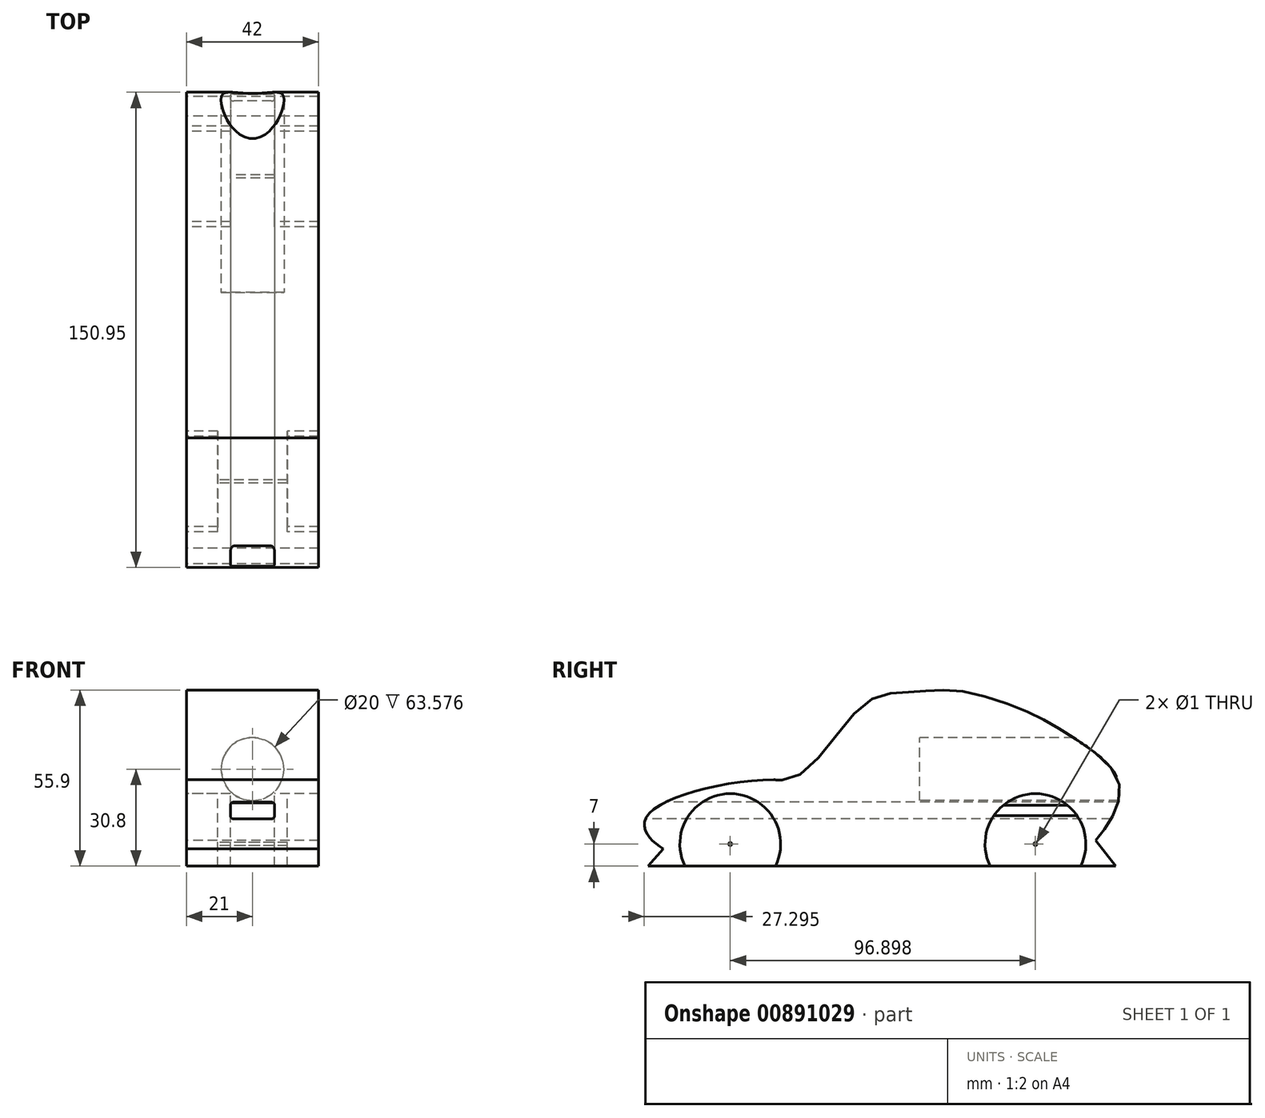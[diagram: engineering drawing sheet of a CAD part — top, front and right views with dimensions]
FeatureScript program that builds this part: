
annotation { "Feature Type Name" : "Feature", "Feature Type Description" : "" }
export const myFeature = defineFeature(function(context is Context, id is Id, definition is map)
    precondition{}
    {
        {
            var Q0;
            Q0=qCreatedBy(makeId("Right.planeOp"),FACE);
            var sketch = newSketch(context, id + "F0", { "sketchPlane" : qUnion([Q0])});
            skArc(sketch, "E0", {"start": v(63.2, 0) * mm, "mid": v(48.81, 23) * mm, "end": v(34.43, 0) * mm});
            skCircle(sketch, "E1", {"center": v(48.81, 7) * mm, "radius": 0.5 * mm});
            skLineSegment(sketch, "E2", {"start": v(-74.19, 0) * mm, "end": v(-69.32, 5.42) * mm});
            skLineSegment(sketch, "E3", {"start": v(74.24, 0) * mm, "end": v(68, 8.2) * mm});
            skLineSegment(sketch, "E4", {"start": v(34.43, 0) * mm, "end": v(63.2, 0) * mm});
            skLineSegment(sketch, "E5", {"start": v(63.2, 0) * mm, "end": v(74.24, 0) * mm});
            skFitSpline(sketch, "E6", {"points": [v(-69.32, 5.42) * mm, v(-74.16, 9.7) * mm, v(-74.86, 15.33) * mm, v(-52.68, 25.37) * mm, v(-23.1, 24.85) * mm], "startDerivative": vector(-34.94, 24.78) * mm, "endDerivative": vector(31.68, -31.68) * mm});
            skFitSpline(sketch, "E7", {"points": [v(68, 8.2) * mm, v(73.36, 16.04) * mm, v(74.77, 28) * mm, v(59.1, 41.91) * mm, v(46.07, 49.13) * mm, v(24.42, 55.65) * mm, v(9.81, 55.3) * mm, v(-5.33, 51.6) * mm, v(-26.85, 28.6) * mm, v(-34.3, 27.45) * mm, v(-34.27, 27.45) * mm], "startDerivative": vector(66.23, 83.04) * mm, "endDerivative": vector(8.76, -0.08) * mm});
            skArc(sketch, "E8", {"start": v(-33.7, 0) * mm, "mid": v(-48.09, 23) * mm, "end": v(-62.47, 0) * mm});
            skLineSegment(sketch, "E9", {"start": v(-74.19, 0) * mm, "end": v(-62.47, 0) * mm});
            skLineSegment(sketch, "E10", {"start": v(-62.47, 0) * mm, "end": v(-33.7, 0) * mm});
            skLineSegment(sketch, "E11", {"start": v(-33.7, 0) * mm, "end": v(34.43, 0) * mm});
            skCircle(sketch, "E12", {"center": v(-48.09, 7) * mm, "radius": 0.5 * mm});
            skSolve(sketch);
        }
        {
            var Q0;
            Q0=makeQuery(id+"F0.imprint","IMPRINT",FACE,{"disambiguationData":[TD([[makeQuery(id+"F0.imprint","IMPRINT",EDGE,{"derivedFrom":sQuery(id+"F0.wireOp",EDGE,"E0")}),-1.0]])]});
            extrude(context, id + "F1", {"entities" : qUnion([Q0]), "depth" : 21 * mm, "offsetDistance" : 25 * mm, "hasSecondDirection" : true, "secondDirectionOppositeDirection" : true, "secondDirectionDepth" : 21 * mm});
        }
        {
            var Q0;
            Q0=makeQuery(id+"F0.imprint","IMPRINT",FACE,{"disambiguationData":[TD([[makeQuery(id+"F0.imprint","IMPRINT",EDGE,{"derivedFrom":sQuery(id+"F0.wireOp",EDGE,"E8")}),1.0]])]});
            extrude(context, id + "F2", {"entities" : qUnion([Q0]), "operationType" : NewBodyOperationType.ADD, "depth" : 11 * mm, "offsetDistance" : 25 * mm, "hasSecondDirection" : true, "secondDirectionOppositeDirection" : true, "secondDirectionDepth" : 11 * mm});
        }
        {
            var Q0;
            Q0=makeQuery(id+"F0.imprint","IMPRINT",FACE,{"disambiguationData":[TD([[makeQuery(id+"F0.imprint","IMPRINT",EDGE,{"derivedFrom":sQuery(id+"F0.wireOp",EDGE,"E0")}),1.0]])]});
            extrude(context, id + "F3", {"entities" : qUnion([Q0]), "operationType" : NewBodyOperationType.ADD, "depth" : 7 * mm, "offsetDistance" : 25 * mm, "hasSecondDirection" : true, "secondDirectionOppositeDirection" : true, "secondDirectionDepth" : 7 * mm});
        }
        {
            var Q0;
            Q0=qCreatedBy(makeId("Front.planeOp"),FACE);
            var sketch = newSketch(context, id + "F4", { "sketchPlane" : qUnion([Q0])});
            skCircle(sketch, "E13", {"center": v(0, 30.8) * mm, "radius": 10 * mm});
            skSolve(sketch);
        }
        {
            var Q0;
            Q0=qSketchRegion(id+"F4",true);
            extrude(context, id + "F5", {"entities" : qUnion([Q0]), "operationType" : NewBodyOperationType.REMOVE, "oppositeDirection" : true, "depth" : 76 * mm, "offsetDistance" : 25 * mm});
        }
        {
            var Q0;
            Q0=qSketchRegion(id+"F4",true);
            extrude(context, id + "F6", {"entities" : qUnion([Q0]), "operationType" : NewBodyOperationType.ADD, "oppositeDirection" : true, "depth" : 12 * mm, "offsetDistance" : 25 * mm});
        }
        {
            var Q0;
            Q0=qCreatedBy(makeId("Front.planeOp"),FACE);
            var sketch = newSketch(context, id + "F7", { "sketchPlane" : qUnion([Q0])});
            skLineSegment(sketch, "E14.bottom", {"start": v(-6, 20.31) * mm, "end": v(6, 20.31) * mm});
            skLineSegment(sketch, "E14.top", {"start": v(-6, 15) * mm, "end": v(6, 15) * mm});
            skLineSegment(sketch, "E14.left", {"start": v(-7, 19.31) * mm, "end": v(-7, 16) * mm});
            skLineSegment(sketch, "E14.right", {"start": v(7, 19.31) * mm, "end": v(7, 16) * mm});
            skPoint(sketch, "E15.visualSharp", {"position": v(-7, 20.31) * mm});
            skArc(sketch, "E15.filletArc", {"start": v(-6, 20.31) * mm, "mid": v(-6.7, 20.02) * mm, "end": v(-7, 19.31) * mm});
            skPoint(sketch, "E16.visualSharp", {"position": v(7, 20.31) * mm});
            skArc(sketch, "E16.filletArc", {"start": v(7, 19.31) * mm, "mid": v(6.7, 20.02) * mm, "end": v(6, 20.31) * mm});
            skPoint(sketch, "E17.visualSharp", {"position": v(7, 15) * mm});
            skArc(sketch, "E17.filletArc", {"start": v(6, 15) * mm, "mid": v(6.7, 15.3) * mm, "end": v(7, 16) * mm});
            skPoint(sketch, "E18.visualSharp", {"position": v(-7, 15) * mm});
            skArc(sketch, "E18.filletArc", {"start": v(-7, 16) * mm, "mid": v(-6.7, 15.3) * mm, "end": v(-6, 15) * mm});
            skSolve(sketch);
        }
        {
            var Q0;
            Q0=qSketchRegion(id+"F7",true);
            extrude(context, id + "F8", {"entities" : qUnion([Q0]), "operationType" : NewBodyOperationType.REMOVE, "oppositeDirection" : true, "depth" : 75 * mm, "offsetDistance" : 25 * mm, "hasSecondDirection" : true, "secondDirectionOppositeDirection" : false, "secondDirectionDepth" : 75 * mm});
        }
    });
